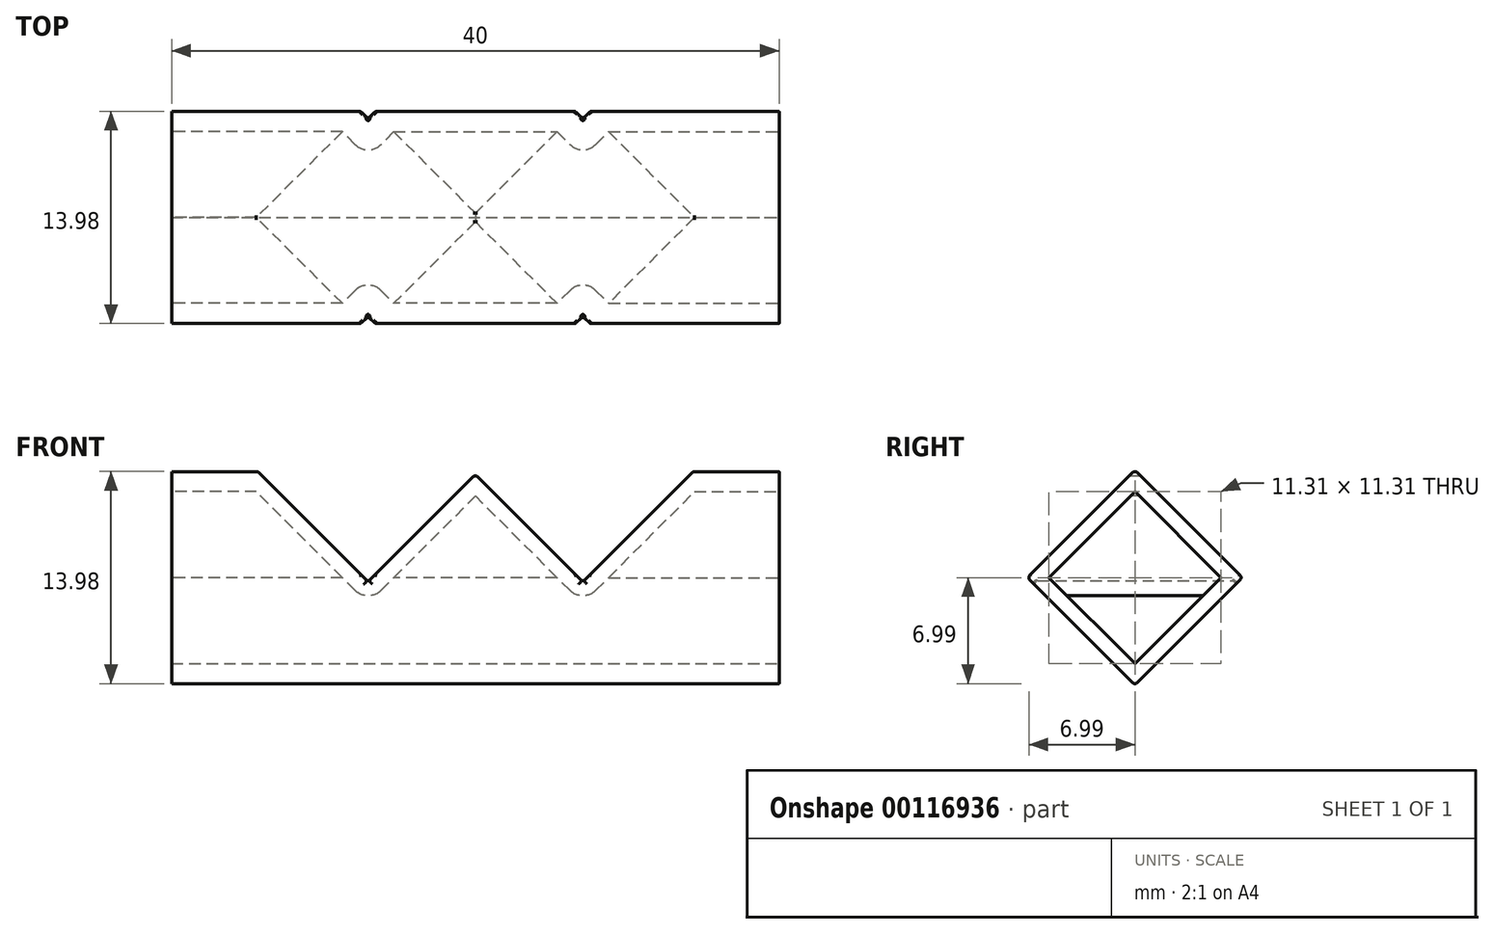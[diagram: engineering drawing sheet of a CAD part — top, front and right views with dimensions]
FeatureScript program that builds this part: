
annotation { "Feature Type Name" : "Feature", "Feature Type Description" : "" }
export const myFeature = defineFeature(function(context is Context, id is Id, definition is map)
    precondition{}
    {
        {
            var Q0;
            Q0=qCreatedBy(makeId("Right.planeOp"),FACE);
            var sketch = newSketch(context, id + "F0", { "sketchPlane" : qUnion([Q0])});
            skLineSegment(sketch, "E0", {"start": v(0, 7.07) * mm, "end": v(-7.07, 0) * mm});
            skLineSegment(sketch, "E1", {"start": v(-7.07, 0) * mm, "end": v(0, -7.07) * mm});
            skLineSegment(sketch, "E2", {"start": v(0, -7.07) * mm, "end": v(7.07, 0) * mm});
            skLineSegment(sketch, "E3", {"start": v(7.07, 0) * mm, "end": v(0, 7.07) * mm});
            skSolve(sketch);
        }
        {
            var Q0;
            Q0 = qSketchRegion(id + "F0", true);
            extrude(context, id + "F1", {"entities" : qUnion([Q0]), "depth" : 20 * mm});
        }
        {
            var Q0;
            Q0=makeQuery(id+"F1.opExtrude","CAP_VERTEX",VERTEX,{"disambiguationData":[OSD([sQuery(id+"F0.wireOp",EDGE,"E0"),sQuery(id+"F0.wireOp",EDGE,"E3")])],"isStart":false});
            var Q1;
            Q1=makeQuery(id+"F1.opExtrude","CAP_VERTEX",VERTEX,{"disambiguationData":[OSD([sQuery(id+"F0.wireOp",EDGE,"E0"),sQuery(id+"F0.wireOp",EDGE,"E3")])],"isStart":true});
            var Q2;
            Q2=makeQuery(id+"F1.opExtrude","CAP_VERTEX",VERTEX,{"disambiguationData":[OSD([sQuery(id+"F0.wireOp",EDGE,"E1"),sQuery(id+"F0.wireOp",EDGE,"E2")])],"isStart":false});
            cPlane(context, id + "F2", {"entities" : qUnion([Q0, Q1, Q2]), "cplaneType" : CPlaneType.THREE_POINT, "offset" : 25 * mm, "width" : 150 * mm, "height" : 150 * mm});
        }
        {
            var Q0;
            Q0=qCreatedBy(id+"F2.planeOp",FACE);
            var sketch = newSketch(context, id + "F3", { "sketchPlane" : qUnion([Q0])});
            skLineSegment(sketch, "E4", {"start": v(0, 0) * mm, "end": v(0, 36.11) * mm, "construction": true});
            skLineSegment(sketch, "E5", {"start": v(-7.07, 0) * mm, "end": v(-14.14, 7.07) * mm, "construction": true});
            skLineSegment(sketch, "E6", {"start": v(-7.07, 0) * mm, "end": v(0, 7.07) * mm, "construction": true});
            skLineSegment(sketch, "E7", {"start": v(-14.14, 7.07) * mm, "end": v(-7.07, 14.14) * mm, "construction": true});
            skLineSegment(sketch, "E8", {"start": v(-7.07, 14.14) * mm, "end": v(0, 7.07) * mm, "construction": true});
            skLineSegment(sketch, "E9.0", {"start": v(-7.07, 14.42) * mm, "end": v(0.28, 7.07) * mm});
            skLineSegment(sketch, "E9.1", {"start": v(-14.42, 7.07) * mm, "end": v(-7.07, 14.42) * mm});
            skLineSegment(sketch, "E9.2", {"start": v(-7.07, -0.28) * mm, "end": v(-14.42, 7.07) * mm});
            skLineSegment(sketch, "E9.3", {"start": v(-7.07, -0.28) * mm, "end": v(0.28, 7.07) * mm});
            skSolve(sketch);
        }
        {
            var Q0;
            Q0 = qSketchRegion(id + "F3", true);
            extrude(context, id + "F4", {"entities" : qUnion([Q0]), "operationType" : NewBodyOperationType.REMOVE, "endBound" : BoundingType.THROUGH_ALL, "oppositeDirection" : true, "depth" : 25 * mm, "hasSecondDirection" : true, "secondDirectionBound" : SecondDirectionBoundingType.THROUGH_ALL, "secondDirectionOppositeDirection" : false, "secondDirectionDepth" : 25 * mm});
        }
        {
            var Q0;
            Q0=qCreatedBy(id+"F2.planeOp",FACE);
            var sketch = newSketch(context, id + "F5", { "sketchPlane" : qUnion([Q0])});
            skLineSegment(sketch, "E10.0", {"start": v(-7.07, 0) * mm, "end": v(-14.14, 7.07) * mm});
            skLineSegment(sketch, "E10.1", {"start": v(-7.07, 0) * mm, "end": v(0, 7.07) * mm});
            skSolve(sketch);
        }
        {
            var Q0;
            Q0=sQuery(id+"F5.wireOp",EDGE,"E10.0");
            var Q1;
            Q1=sQuery(id+"F5.wireOp",EDGE,"E10.1");
            extrude(context, id + "F6", {"bodyType" : ToolBodyType.SURFACE, "surfaceEntities" : qUnion([Q0, Q1]), "depth" : 15 * mm, "hasSecondDirection" : true, "secondDirectionOppositeDirection" : true, "secondDirectionDepth" : 15 * mm});
        }
        {
            var Q0;
            Q0=makeQuery(id+"F1.opExtrude","SWEPT_BODY",BODY,{"disambiguationData":[OSD([sQuery(id+"F0.wireOp",EDGE,"E0"),sQuery(id+"F0.wireOp",EDGE,"E1"),sQuery(id+"F0.wireOp",EDGE,"E2"),sQuery(id+"F0.wireOp",EDGE,"E3")])]});
            var Q1;
            Q1=makeQuery(id+"F1.opExtrude","CAP_FACE",FACE,{"disambiguationData":[OSD([sQuery(id+"F0.wireOp",EDGE,"E0"),sQuery(id+"F0.wireOp",EDGE,"E1"),sQuery(id+"F0.wireOp",EDGE,"E2"),sQuery(id+"F0.wireOp",EDGE,"E3")])],"isStart":true});
            mirror(context, id + "F7", {"operationType" : NewBodyOperationType.ADD, "entities" : qUnion([Q0]), "mirrorPlane" : qUnion([Q1])});
        }
        {
            var Q0;
            Q0=makeQuery(id+"F4.boolean.opBoolean","COPY",EDGE,{"derivedFrom":makeQuery(id+"F4.opExtrude","SWEPT_EDGE",EDGE,{"disambiguationData":[OSD([sQuery(id+"F3.wireOp",EDGE,"E9.2"),sQuery(id+"F3.wireOp",EDGE,"E9.3")])]})});
            var Q1;
            Q1=makeQuery(id+"F4.boolean.opBoolean","INTERSECT",EDGE,{"derivedFrom":[makeQuery(id+"F1.opExtrude","SWEPT_FACE",FACE,{"disambiguationData":[OSD([sQuery(id+"F0.wireOp",EDGE,"E0")])]}),makeQuery(id+"F4.opExtrude","SWEPT_FACE",FACE,{"disambiguationData":[OSD([sQuery(id+"F3.wireOp",EDGE,"E9.3")])]})]});
            var Q2;
            Q2=makeQuery(id+"F4.boolean.opBoolean","INTERSECT",EDGE,{"derivedFrom":[makeQuery(id+"F1.opExtrude","SWEPT_FACE",FACE,{"disambiguationData":[OSD([sQuery(id+"F0.wireOp",EDGE,"E3")])]}),makeQuery(id+"F4.opExtrude","SWEPT_FACE",FACE,{"disambiguationData":[OSD([sQuery(id+"F3.wireOp",EDGE,"E9.3")])]})]});
            var Q3;
            {var subQ0=makeQuery(id+"F4.boolean.opBoolean","INTERSECT",EDGE,{"derivedFrom":[makeQuery(id+"F1.opExtrude","CAP_FACE",FACE,{"disambiguationData":[OSD([sQuery(id+"F0.wireOp",EDGE,"E0"),sQuery(id+"F0.wireOp",EDGE,"E1"),sQuery(id+"F0.wireOp",EDGE,"E2"),sQuery(id+"F0.wireOp",EDGE,"E3")])],"isStart":true}),makeQuery(id+"F4.opExtrude","SWEPT_FACE",FACE,{"disambiguationData":[OSD([sQuery(id+"F3.wireOp",EDGE,"E9.3")])]})]});Q3=makeQuery(id+"F7.boolean.opBoolean","MERGE",EDGE,{"derivedFrom":[subQ0,makeQuery(id+"F7.opPattern","COPY",EDGE,{"derivedFrom":subQ0,"instanceName":"1"})]});}
            var Q4;
            Q4=makeQuery(id+"F4.boolean.opBoolean","INTERSECT",EDGE,{"derivedFrom":[makeQuery(id+"F1.opExtrude","SWEPT_FACE",FACE,{"disambiguationData":[OSD([sQuery(id+"F0.wireOp",EDGE,"E1")])]}),makeQuery(id+"F4.opExtrude","SWEPT_FACE",FACE,{"disambiguationData":[OSD([sQuery(id+"F3.wireOp",EDGE,"E9.3")])]})]});
            var Q5;
            Q5=makeQuery(id+"F4.boolean.opBoolean","INTERSECT",EDGE,{"derivedFrom":[makeQuery(id+"F1.opExtrude","SWEPT_FACE",FACE,{"disambiguationData":[OSD([sQuery(id+"F0.wireOp",EDGE,"E2")])]}),makeQuery(id+"F4.opExtrude","SWEPT_FACE",FACE,{"disambiguationData":[OSD([sQuery(id+"F3.wireOp",EDGE,"E9.3")])]})]});
            var Q6;
            Q6=makeQuery(id+"F4.boolean.opBoolean","INTERSECT",EDGE,{"derivedFrom":[makeQuery(id+"F1.opExtrude","SWEPT_FACE",FACE,{"disambiguationData":[OSD([sQuery(id+"F0.wireOp",EDGE,"E2")])]}),makeQuery(id+"F4.opExtrude","SWEPT_FACE",FACE,{"disambiguationData":[OSD([sQuery(id+"F3.wireOp",EDGE,"E9.2")])]})]});
            var Q7;
            Q7=makeQuery(id+"F4.boolean.opBoolean","INTERSECT",EDGE,{"derivedFrom":[makeQuery(id+"F1.opExtrude","SWEPT_FACE",FACE,{"disambiguationData":[OSD([sQuery(id+"F0.wireOp",EDGE,"E1")])]}),makeQuery(id+"F4.opExtrude","SWEPT_FACE",FACE,{"disambiguationData":[OSD([sQuery(id+"F3.wireOp",EDGE,"E9.2")])]})]});
            var Q8;
            Q8=makeQuery(id+"F4.boolean.opBoolean","INTERSECT",EDGE,{"derivedFrom":[makeQuery(id+"F1.opExtrude","SWEPT_FACE",FACE,{"disambiguationData":[OSD([sQuery(id+"F0.wireOp",EDGE,"E0")])]}),makeQuery(id+"F4.opExtrude","SWEPT_FACE",FACE,{"disambiguationData":[OSD([sQuery(id+"F3.wireOp",EDGE,"E9.2")])]})]});
            var Q9;
            Q9=makeQuery(id+"F4.boolean.opBoolean","INTERSECT",EDGE,{"derivedFrom":[makeQuery(id+"F1.opExtrude","SWEPT_FACE",FACE,{"disambiguationData":[OSD([sQuery(id+"F0.wireOp",EDGE,"E3")])]}),makeQuery(id+"F4.opExtrude","SWEPT_FACE",FACE,{"disambiguationData":[OSD([sQuery(id+"F3.wireOp",EDGE,"E9.2")])]})]});
            var Q10;
            Q10=makeQuery(id+"F1.opExtrude","SWEPT_EDGE",EDGE,{"disambiguationData":[OSD([sQuery(id+"F0.wireOp",EDGE,"E0"),sQuery(id+"F0.wireOp",EDGE,"E3")])]});
            var Q11;
            {var subQ0=sQuery(id+"F0.wireOp",EDGE,"E3");var subQ1=sQuery(id+"F0.wireOp",EDGE,"E2");Q11=makeQuery(id+"F4.boolean.opBoolean","SPLIT",EDGE,{"disambiguationData":[TD([makeQuery(id+"F4.opExtrude","SWEPT_FACE",FACE,{"disambiguationData":[OSD([sQuery(id+"F3.wireOp",EDGE,"E9.2")])]})])],"derivedFrom":makeQuery(id+"F1.opExtrude","SWEPT_EDGE",EDGE,{"disambiguationData":[OSD([subQ1,subQ0])]})});}
            var Q12;
            {var subQ0=sQuery(id+"F0.wireOp",EDGE,"E0");var subQ1=sQuery(id+"F0.wireOp",EDGE,"E1");Q12=makeQuery(id+"F4.boolean.opBoolean","SPLIT",EDGE,{"disambiguationData":[TD([makeQuery(id+"F4.opExtrude","SWEPT_FACE",FACE,{"disambiguationData":[OSD([sQuery(id+"F3.wireOp",EDGE,"E9.2")])]})])],"derivedFrom":makeQuery(id+"F1.opExtrude","SWEPT_EDGE",EDGE,{"disambiguationData":[OSD([subQ0,subQ1])]})});}
            var Q13;
            {var subQ0=sQuery(id+"F0.wireOp",EDGE,"E0");var subQ1=sQuery(id+"F0.wireOp",EDGE,"E1");var subQ2=makeQuery(id+"F4.boolean.opBoolean","SPLIT",EDGE,{"disambiguationData":[TD([makeQuery(id+"F4.opExtrude","SWEPT_FACE",FACE,{"disambiguationData":[OSD([sQuery(id+"F3.wireOp",EDGE,"E9.3")])]})])],"derivedFrom":makeQuery(id+"F1.opExtrude","SWEPT_EDGE",EDGE,{"disambiguationData":[OSD([subQ0,subQ1])]})});Q13=makeQuery(id+"F7.boolean.opBoolean","MERGE",EDGE,{"derivedFrom":[subQ2,makeQuery(id+"F7.opPattern","COPY",EDGE,{"derivedFrom":subQ2,"instanceName":"1"})]});}
            var Q14;
            {var subQ0=sQuery(id+"F0.wireOp",EDGE,"E0");var subQ1=sQuery(id+"F0.wireOp",EDGE,"E1");Q14=makeQuery(id+"F7.opPattern","COPY",EDGE,{"derivedFrom":makeQuery(id+"F4.boolean.opBoolean","SPLIT",EDGE,{"disambiguationData":[TD([makeQuery(id+"F4.opExtrude","SWEPT_FACE",FACE,{"disambiguationData":[OSD([sQuery(id+"F3.wireOp",EDGE,"E9.2")])]})])],"derivedFrom":makeQuery(id+"F1.opExtrude","SWEPT_EDGE",EDGE,{"disambiguationData":[OSD([subQ0,subQ1])]})}),"instanceName":"1"});}
            var Q15;
            Q15=makeQuery(id+"F7.opPattern","COPY",EDGE,{"derivedFrom":makeQuery(id+"F4.boolean.opBoolean","INTERSECT",EDGE,{"derivedFrom":[makeQuery(id+"F1.opExtrude","SWEPT_FACE",FACE,{"disambiguationData":[OSD([sQuery(id+"F0.wireOp",EDGE,"E1")])]}),makeQuery(id+"F4.opExtrude","SWEPT_FACE",FACE,{"disambiguationData":[OSD([sQuery(id+"F3.wireOp",EDGE,"E9.2")])]})]}),"instanceName":"1"});
            var Q16;
            Q16=makeQuery(id+"F7.opPattern","COPY",EDGE,{"derivedFrom":makeQuery(id+"F4.boolean.opBoolean","INTERSECT",EDGE,{"derivedFrom":[makeQuery(id+"F1.opExtrude","SWEPT_FACE",FACE,{"disambiguationData":[OSD([sQuery(id+"F0.wireOp",EDGE,"E1")])]}),makeQuery(id+"F4.opExtrude","SWEPT_FACE",FACE,{"disambiguationData":[OSD([sQuery(id+"F3.wireOp",EDGE,"E9.3")])]})]}),"instanceName":"1"});
            var Q17;
            Q17=makeQuery(id+"F7.opPattern","COPY",EDGE,{"derivedFrom":makeQuery(id+"F4.boolean.opBoolean","INTERSECT",EDGE,{"derivedFrom":[makeQuery(id+"F1.opExtrude","SWEPT_FACE",FACE,{"disambiguationData":[OSD([sQuery(id+"F0.wireOp",EDGE,"E0")])]}),makeQuery(id+"F4.opExtrude","SWEPT_FACE",FACE,{"disambiguationData":[OSD([sQuery(id+"F3.wireOp",EDGE,"E9.2")])]})]}),"instanceName":"1"});
            var Q18;
            Q18=makeQuery(id+"F7.opPattern","COPY",EDGE,{"derivedFrom":makeQuery(id+"F4.boolean.opBoolean","INTERSECT",EDGE,{"derivedFrom":[makeQuery(id+"F1.opExtrude","SWEPT_FACE",FACE,{"disambiguationData":[OSD([sQuery(id+"F0.wireOp",EDGE,"E0")])]}),makeQuery(id+"F4.opExtrude","SWEPT_FACE",FACE,{"disambiguationData":[OSD([sQuery(id+"F3.wireOp",EDGE,"E9.3")])]})]}),"instanceName":"1"});
            var Q19;
            Q19=makeQuery(id+"F7.opPattern","COPY",EDGE,{"derivedFrom":makeQuery(id+"F4.boolean.opBoolean","INTERSECT",EDGE,{"derivedFrom":[makeQuery(id+"F1.opExtrude","SWEPT_FACE",FACE,{"disambiguationData":[OSD([sQuery(id+"F0.wireOp",EDGE,"E3")])]}),makeQuery(id+"F4.opExtrude","SWEPT_FACE",FACE,{"disambiguationData":[OSD([sQuery(id+"F3.wireOp",EDGE,"E9.3")])]})]}),"instanceName":"1"});
            var Q20;
            Q20=makeQuery(id+"F7.opPattern","COPY",EDGE,{"derivedFrom":makeQuery(id+"F4.boolean.opBoolean","COPY",EDGE,{"derivedFrom":makeQuery(id+"F4.opExtrude","SWEPT_EDGE",EDGE,{"disambiguationData":[OSD([sQuery(id+"F3.wireOp",EDGE,"E9.2"),sQuery(id+"F3.wireOp",EDGE,"E9.3")])]})}),"instanceName":"1"});
            var Q21;
            Q21=makeQuery(id+"F7.opPattern","COPY",EDGE,{"derivedFrom":makeQuery(id+"F4.boolean.opBoolean","INTERSECT",EDGE,{"derivedFrom":[makeQuery(id+"F1.opExtrude","SWEPT_FACE",FACE,{"disambiguationData":[OSD([sQuery(id+"F0.wireOp",EDGE,"E2")])]}),makeQuery(id+"F4.opExtrude","SWEPT_FACE",FACE,{"disambiguationData":[OSD([sQuery(id+"F3.wireOp",EDGE,"E9.2")])]})]}),"instanceName":"1"});
            var Q22;
            Q22=makeQuery(id+"F7.opPattern","COPY",EDGE,{"derivedFrom":makeQuery(id+"F4.boolean.opBoolean","INTERSECT",EDGE,{"derivedFrom":[makeQuery(id+"F1.opExtrude","SWEPT_FACE",FACE,{"disambiguationData":[OSD([sQuery(id+"F0.wireOp",EDGE,"E2")])]}),makeQuery(id+"F4.opExtrude","SWEPT_FACE",FACE,{"disambiguationData":[OSD([sQuery(id+"F3.wireOp",EDGE,"E9.3")])]})]}),"instanceName":"1"});
            var Q23;
            Q23=makeQuery(id+"F7.opPattern","COPY",EDGE,{"derivedFrom":makeQuery(id+"F4.boolean.opBoolean","INTERSECT",EDGE,{"derivedFrom":[makeQuery(id+"F1.opExtrude","SWEPT_FACE",FACE,{"disambiguationData":[OSD([sQuery(id+"F0.wireOp",EDGE,"E3")])]}),makeQuery(id+"F4.opExtrude","SWEPT_FACE",FACE,{"disambiguationData":[OSD([sQuery(id+"F3.wireOp",EDGE,"E9.2")])]})]}),"instanceName":"1"});
            var Q24;
            Q24=makeQuery(id+"F7.opPattern","COPY",EDGE,{"derivedFrom":makeQuery(id+"F1.opExtrude","SWEPT_EDGE",EDGE,{"disambiguationData":[OSD([sQuery(id+"F0.wireOp",EDGE,"E0"),sQuery(id+"F0.wireOp",EDGE,"E3")])]}),"instanceName":"1"});
            var Q25;
            {var subQ0=sQuery(id+"F0.wireOp",EDGE,"E3");var subQ1=sQuery(id+"F0.wireOp",EDGE,"E2");Q25=makeQuery(id+"F7.opPattern","COPY",EDGE,{"derivedFrom":makeQuery(id+"F4.boolean.opBoolean","SPLIT",EDGE,{"disambiguationData":[TD([makeQuery(id+"F4.opExtrude","SWEPT_FACE",FACE,{"disambiguationData":[OSD([sQuery(id+"F3.wireOp",EDGE,"E9.2")])]})])],"derivedFrom":makeQuery(id+"F1.opExtrude","SWEPT_EDGE",EDGE,{"disambiguationData":[OSD([subQ1,subQ0])]})}),"instanceName":"1"});}
            var Q26;
            {var subQ0=sQuery(id+"F0.wireOp",EDGE,"E3");var subQ1=sQuery(id+"F0.wireOp",EDGE,"E2");var subQ2=makeQuery(id+"F4.boolean.opBoolean","SPLIT",EDGE,{"disambiguationData":[TD([makeQuery(id+"F4.opExtrude","SWEPT_FACE",FACE,{"disambiguationData":[OSD([sQuery(id+"F3.wireOp",EDGE,"E9.3")])]})])],"derivedFrom":makeQuery(id+"F1.opExtrude","SWEPT_EDGE",EDGE,{"disambiguationData":[OSD([subQ1,subQ0])]})});Q26=makeQuery(id+"F7.boolean.opBoolean","MERGE",EDGE,{"derivedFrom":[subQ2,makeQuery(id+"F7.opPattern","COPY",EDGE,{"derivedFrom":subQ2,"instanceName":"1"})]});}
            var Q27;
            {var subQ0=makeQuery(id+"F1.opExtrude","SWEPT_EDGE",EDGE,{"disambiguationData":[OSD([sQuery(id+"F0.wireOp",EDGE,"E1"),sQuery(id+"F0.wireOp",EDGE,"E2")])]});Q27=makeQuery(id+"F7.boolean.opBoolean","MERGE",EDGE,{"derivedFrom":[subQ0,makeQuery(id+"F7.opPattern","COPY",EDGE,{"derivedFrom":subQ0,"instanceName":"1"})]});}
            fillet(context, id + "F8", {"entities" : qUnion([Q0, Q1, Q2, Q3, Q4, Q5, Q6, Q7, Q8, Q9, Q10, Q11, Q12, Q13, Q14, Q15, Q16, Q17, Q18, Q19, Q20, Q21, Q22, Q23, Q24, Q25, Q26, Q27]), "radius" : 0.2 * mm, "tangentPropagation" : true, "allowEdgeOverflow" : false});
        }
        {
            var Q0;
            Q0=makeQuery(id+"F1.opExtrude","CAP_FACE",FACE,{"disambiguationData":[OSD([sQuery(id+"F0.wireOp",EDGE,"E0"),sQuery(id+"F0.wireOp",EDGE,"E1"),sQuery(id+"F0.wireOp",EDGE,"E2"),sQuery(id+"F0.wireOp",EDGE,"E3")])],"isStart":false});
            var Q1;
            Q1=makeQuery(id+"F7.opPattern","COPY",FACE,{"derivedFrom":makeQuery(id+"F1.opExtrude","CAP_FACE",FACE,{"disambiguationData":[OSD([sQuery(id+"F0.wireOp",EDGE,"E0"),sQuery(id+"F0.wireOp",EDGE,"E1"),sQuery(id+"F0.wireOp",EDGE,"E2"),sQuery(id+"F0.wireOp",EDGE,"E3")])],"isStart":false}),"instanceName":"1"});
            shell(context, id + "F9", {"entities" : qUnion([Q0, Q1]), "thickness" : 1 * mm});
        }
    });
